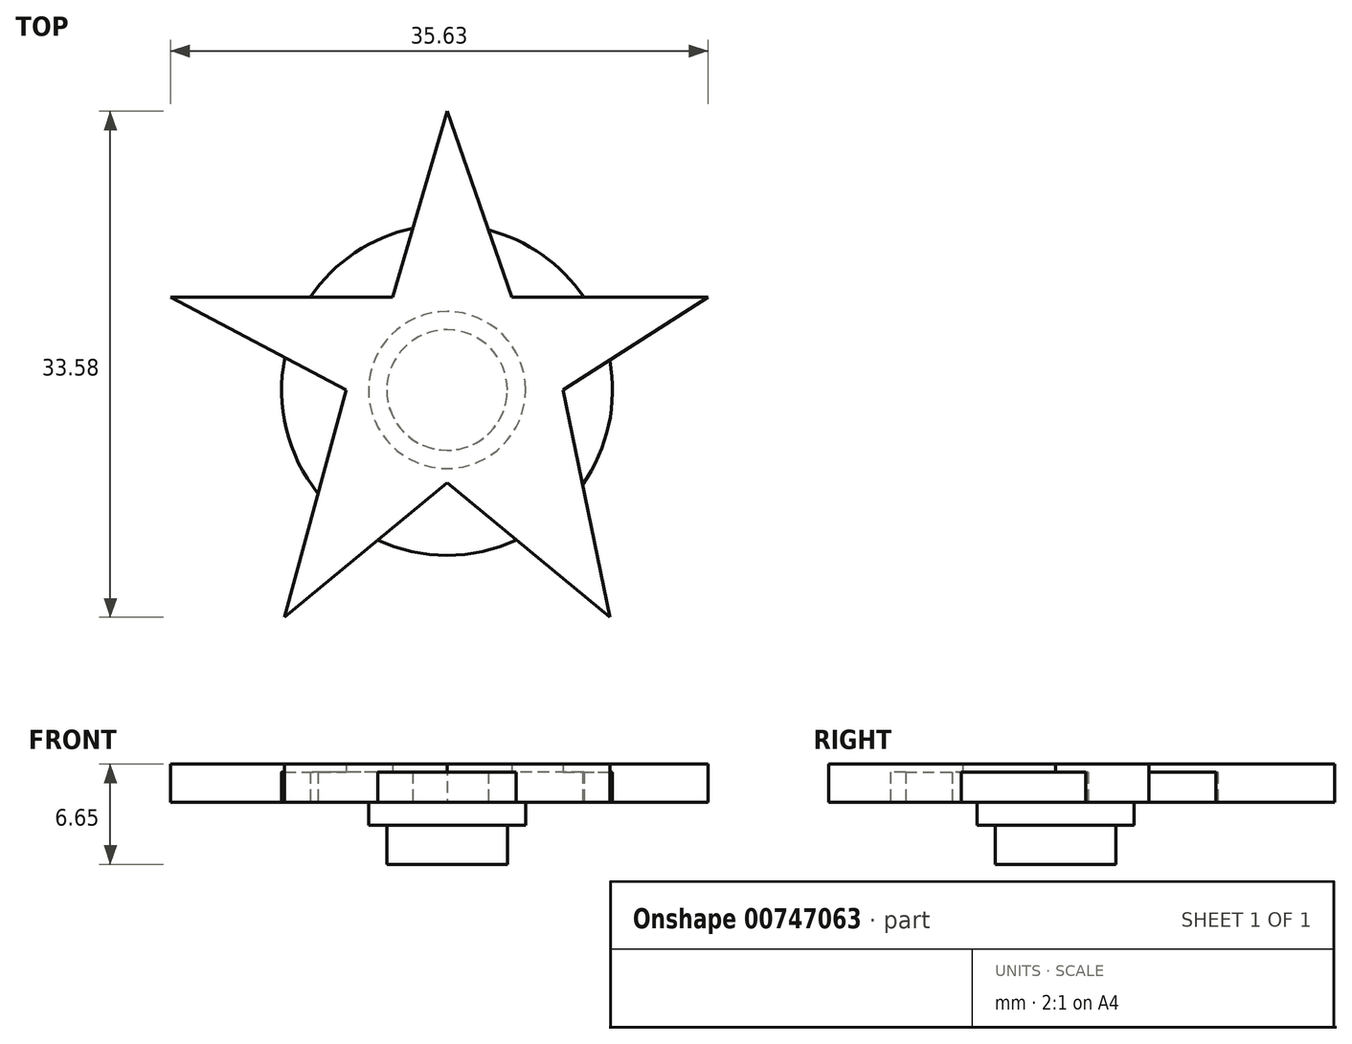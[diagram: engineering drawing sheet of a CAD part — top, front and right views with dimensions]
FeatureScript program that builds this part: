
annotation { "Feature Type Name" : "Feature", "Feature Type Description" : "" }
export const myFeature = defineFeature(function(context is Context, id is Id, definition is map)
    precondition{}
    {
        {
            var Q0;
            Q0=qCreatedBy(makeId("Top.planeOp"),FACE);
            var sketch = newSketch(context, id + "F0", { "sketchPlane" : qUnion([Q0])});
            skCircle(sketch, "E0", {"center": v(0, 0) * mm, "radius": 10.97 * mm});
            skSolve(sketch);
        }
        {
            var Q0;
            Q0 = qSketchRegion(id + "F0", true);
            extrude(context, id + "F1", {"entities" : qUnion([Q0]), "depth" : 2 * mm, "offsetDistance" : 25.4 * mm});
        }
        {
            var Q0;
            Q0=makeQuery(id+"F1.opExtrude","CAP_FACE",FACE,{"disambiguationData":[OSD([sQuery(id+"F0.wireOp",EDGE,"E0")])],"isStart":true});
            var sketch = newSketch(context, id + "F2", { "sketchPlane" : qUnion([Q0])});
            skCircle(sketch, "E1", {"center": v(0, 0) * mm, "radius": 5.2 * mm});
            skSolve(sketch);
        }
        {
            var Q0;
            Q0 = qSketchRegion(id + "F2", true);
            extrude(context, id + "F3", {"entities" : qUnion([Q0]), "operationType" : NewBodyOperationType.ADD, "depth" : 1.52 * mm, "offsetDistance" : 25.4 * mm});
        }
        {
            var Q0;
            Q0=qCreatedBy(makeId("Top.planeOp"),FACE);
            var sketch = newSketch(context, id + "F4", { "sketchPlane" : qUnion([Q0])});
            skCircle(sketch, "E2", {"center": v(0, 0) * mm, "radius": 4 * mm});
            skSolve(sketch);
        }
        {
            var Q0;
            Q0 = qSketchRegion(id + "F4", true);
            extrude(context, id + "F5", {"entities" : qUnion([Q0]), "operationType" : NewBodyOperationType.ADD, "oppositeDirection" : true, "depth" : 4.11 * mm, "offsetDistance" : 25.4 * mm});
        }
        {
            var Q0;
            Q0=qCreatedBy(makeId("Top.planeOp"),FACE);
            var sketch = newSketch(context, id + "F6", { "sketchPlane" : qUnion([Q0])});
            skCircle(sketch, "E3", {"center": v(0, 0) * mm, "radius": 19.05 * mm});
            skSolve(sketch);
        }
        {
            var Q0;
            Q0=makeQuery(id+"F6.imprint","IMPRINT",FACE,{"disambiguationData":[TD([[makeQuery(id+"F6.imprint","IMPRINT",EDGE,{"derivedFrom":sQuery(id+"F6.wireOp",EDGE,"E3")}),1.0]])]});
            var sketch = newSketch(context, id + "F7", { "sketchPlane" : qUnion([Q0])});
            skLineSegment(sketch, "E4", {"start": v(0, 18.5) * mm, "end": v(4.28, 6.17) * mm});
            skLineSegment(sketch, "E5", {"start": v(4.28, 6.17) * mm, "end": v(17.3, 6.17) * mm});
            skLineSegment(sketch, "E6", {"start": v(17.3, 6.17) * mm, "end": v(7.7, 0) * mm});
            skLineSegment(sketch, "E7", {"start": v(7.7, 0) * mm, "end": v(10.8, -15.08) * mm});
            skLineSegment(sketch, "E8", {"start": v(10.8, -15.08) * mm, "end": v(0, -6.17) * mm});
            skLineSegment(sketch, "E9", {"start": v(0, -6.17) * mm, "end": v(-10.8, -15.08) * mm});
            skLineSegment(sketch, "E10", {"start": v(-10.8, -15.08) * mm, "end": v(-6.68, 0) * mm});
            skLineSegment(sketch, "E11", {"start": v(-6.68, 0) * mm, "end": v(-18.33, 6.17) * mm});
            skLineSegment(sketch, "E12", {"start": v(-18.33, 6.17) * mm, "end": v(-3.6, 6.17) * mm});
            skLineSegment(sketch, "E13", {"start": v(-3.6, 6.17) * mm, "end": v(0, 18.5) * mm});
            skSolve(sketch);
        }
        {
            var Q0;
            Q0 = qSketchRegion(id + "F7", true);
            extrude(context, id + "F8", {"entities" : qUnion([Q0]), "operationType" : NewBodyOperationType.ADD, "depth" : 2.54 * mm, "offsetDistance" : 25.4 * mm});
        }
    });
